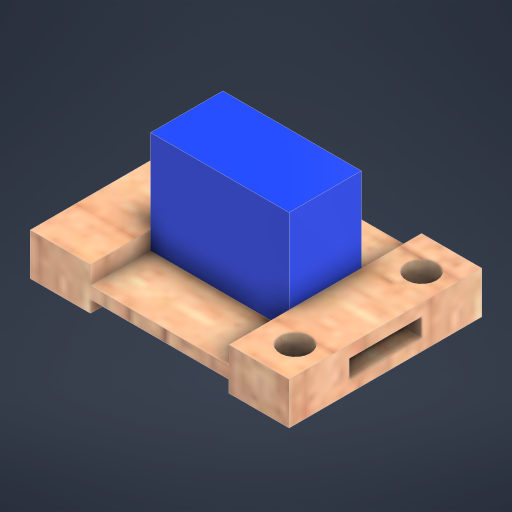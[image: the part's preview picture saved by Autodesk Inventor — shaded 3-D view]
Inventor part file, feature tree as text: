
AUTODESK INVENTOR PART (.ipt)
format: ipt  version: 2023.2 (Build 272271000, 271)  size: 462,848 bytes
history: native  units: mm
features: sketch x6, extrude x1
ambient origin geometry x8: Origin, YZ Plane, XZ Plane, XY Plane, X Axis, Y Axis, Z Axis, Center Point
bodies: Body1 (feature_tree)
feature tree (7):
  sketch  "Sketch1"  dims[d230=31.0mm d231=12.0mm]
  extrude  "Extrusion26"  Depth=12.0mm
  sketch  "Sketch2"  dims[d232=23.0mm]
  sketch  "Sketch3"  dims[d234=4.0mm]
  sketch  "Sketch5"  dims[d235=3.0mm d236=0.0mm]
  sketch  "Sketch7"  dims[d237=19.0mm d238=4.0mm d239=0.0mm d240=0.0mm]
  sketch  "Sketch22"  dims[d241=10.0mm d242=32.0mm d243=10.0mm d244=32.0mm d245=2.0mm d246=0.0mm d247=2.0mm d248=0.0mm d251=3.0mm d252=0.0mm d253=2.0mm d254=0.0mm d255=12.0mm d256=6.0mm d257=6.0mm d258=4.0mm d259=0.0mm d260=5.0mm d261=3.5mm d262=3.0mm d263=0.0mm d266=2.0mm d267=6.0mm d268=6.0mm d269=6.0mm d270=0.0mm d271=5.0mm d272=5.0mm d273=21.0mm d274=5.5mm d275=8.0mm d276=0.0mm d9=0.5mm d10=0.872665mm d11=0.5mm d12=0.872665mm d13=0.5mm d14=0.872665mm d27=0.5mm d28=0.872665mm d29=0.5mm d30=0.872665mm d88=0.5mm d89=0.872665mm d90=0.5mm d91=0.872665mm d116=0.5mm d117=0.872665mm d118=0.5mm d119=0.872665mm d154=0.5mm d155=0.872665mm d156=0.5mm d157=0.872665mm d181=0.5mm d182=0.872665mm d183=0.5mm d184=0.872665mm d221=0.5mm d222=0.872665mm d223=0.5mm d224=0.872665mm]
